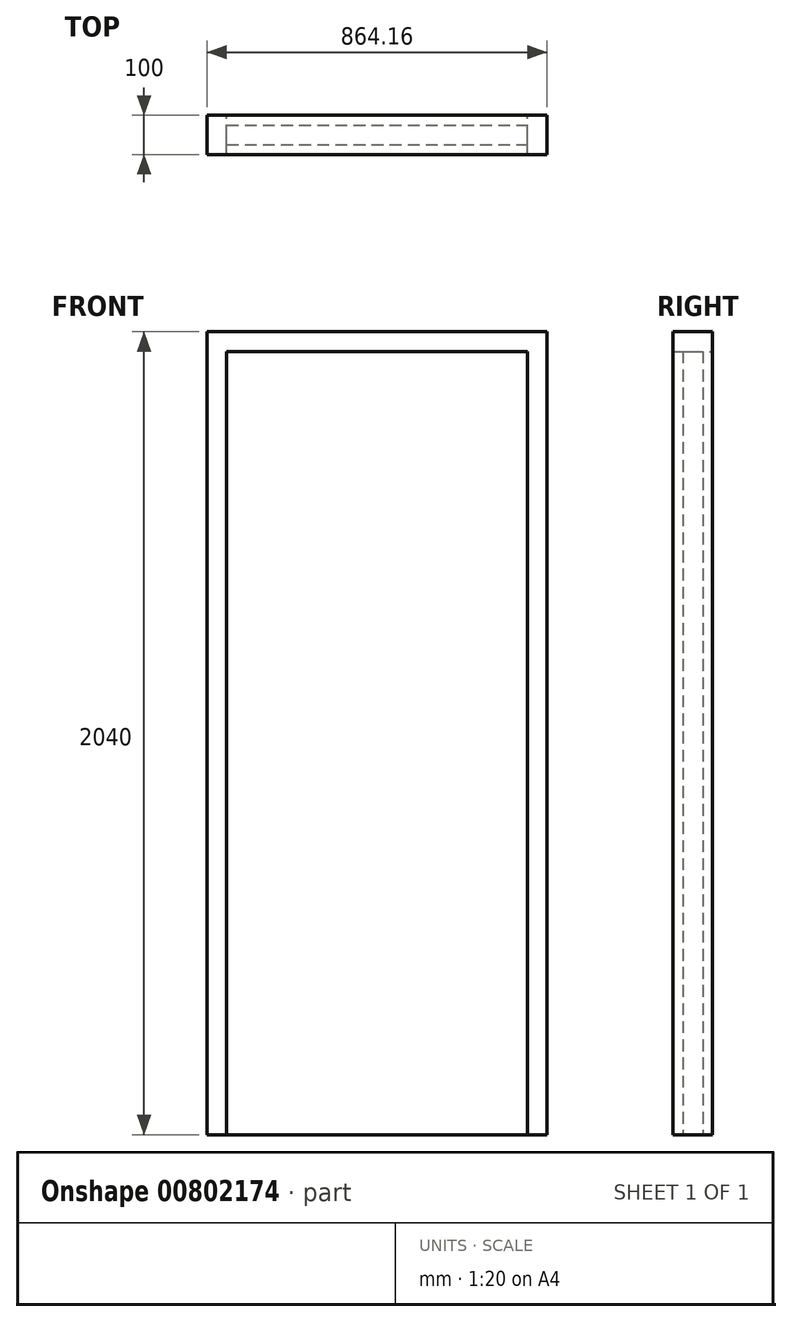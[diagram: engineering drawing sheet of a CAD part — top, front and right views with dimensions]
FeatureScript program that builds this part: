
annotation { "Feature Type Name" : "Feature", "Feature Type Description" : "" }
export const myFeature = defineFeature(function(context is Context, id is Id, definition is map)
    precondition{}
    {
        {
            var Q0;
            Q0=qCreatedBy(makeId("Front.planeOp"),FACE);
            var sketch = newSketch(context, id + "F0", { "sketchPlane" : qUnion([Q0])});
            skLineSegment(sketch, "E0.bottom", {"start": v(-416.93, 1034) * mm, "end": v(447.23, 1034) * mm});
            skLineSegment(sketch, "E0.left", {"start": v(-416.93, 1034) * mm, "end": v(-416.93, -1006) * mm});
            skLineSegment(sketch, "E0.right", {"start": v(447.23, 1034) * mm, "end": v(447.23, -1006) * mm});
            skLineSegment(sketch, "E1.0", {"start": v(-366.93, 984) * mm, "end": v(-366.93, -1006) * mm});
            skLineSegment(sketch, "E1.1", {"start": v(-366.93, 984) * mm, "end": v(397.23, 984) * mm});
            skLineSegment(sketch, "E1.2", {"start": v(397.23, 984) * mm, "end": v(397.23, -1006) * mm});
            skLineSegment(sketch, "E2", {"start": v(-416.93, -1006) * mm, "end": v(-366.93, -1006) * mm});
            skLineSegment(sketch, "E3", {"start": v(397.23, -1006) * mm, "end": v(447.23, -1006) * mm});
            skSolve(sketch);
        }
        {
            var Q0;
            Q0 = qSketchRegion(id + "F0", true);
            extrude(context, id + "F1", {"entities" : qUnion([Q0]), "depth" : 100 * mm, "offsetDistance" : 25 * mm});
        }
        {
            var Q0;
            Q0=makeQuery(id+"F1.opExtrude","CAP_FACE",FACE,{"disambiguationData":[OSD([sQuery(id+"F0.wireOp",EDGE,"E0.bottom"),sQuery(id+"F0.wireOp",EDGE,"E0.left"),sQuery(id+"F0.wireOp",EDGE,"E0.right"),sQuery(id+"F0.wireOp",EDGE,"E1.0"),sQuery(id+"F0.wireOp",EDGE,"E1.1"),sQuery(id+"F0.wireOp",EDGE,"E1.2"),sQuery(id+"F0.wireOp",EDGE,"E2"),sQuery(id+"F0.wireOp",EDGE,"E3")])],"isStart":false});
            var Q1;
            Q1=makeQuery(id+"F1.opExtrude","CAP_FACE",FACE,{"disambiguationData":[OSD([sQuery(id+"F0.wireOp",EDGE,"E0.bottom"),sQuery(id+"F0.wireOp",EDGE,"E0.left"),sQuery(id+"F0.wireOp",EDGE,"E0.right"),sQuery(id+"F0.wireOp",EDGE,"E1.0"),sQuery(id+"F0.wireOp",EDGE,"E1.1"),sQuery(id+"F0.wireOp",EDGE,"E1.2"),sQuery(id+"F0.wireOp",EDGE,"E2"),sQuery(id+"F0.wireOp",EDGE,"E3")])],"isStart":true});
            cPlane(context, id + "F2", {"entities" : qUnion([Q0, Q1]), "cplaneType" : CPlaneType.MID_PLANE, "offset" : 25 * mm, "width" : 150 * mm, "height" : 150 * mm});
        }
        {
            var Q0;
            Q0=qCreatedBy(id+"F2.planeOp",FACE);
            var sketch = newSketch(context, id + "F3", { "sketchPlane" : qUnion([Q0])});
            skLineSegment(sketch, "E4.0", {"start": v(397.23, 984) * mm, "end": v(397.23, -1006) * mm});
            skLineSegment(sketch, "E4.1", {"start": v(-366.93, 984) * mm, "end": v(-366.93, -1006) * mm});
            skLineSegment(sketch, "E4.2", {"start": v(-366.93, 984) * mm, "end": v(397.23, 984) * mm});
            skLineSegment(sketch, "E5", {"start": v(397.23, -1006) * mm, "end": v(-366.93, -1006) * mm});
            skSolve(sketch);
        }
        {
            var Q0;
            Q0 = qSketchRegion(id + "F3", true);
            extrude(context, id + "F4", {"entities" : qUnion([Q0]), "depth" : 25 * mm, "offsetDistance" : 25 * mm, "hasSecondDirection" : true, "secondDirectionOppositeDirection" : true, "secondDirectionDepth" : 25 * mm});
        }
    });
